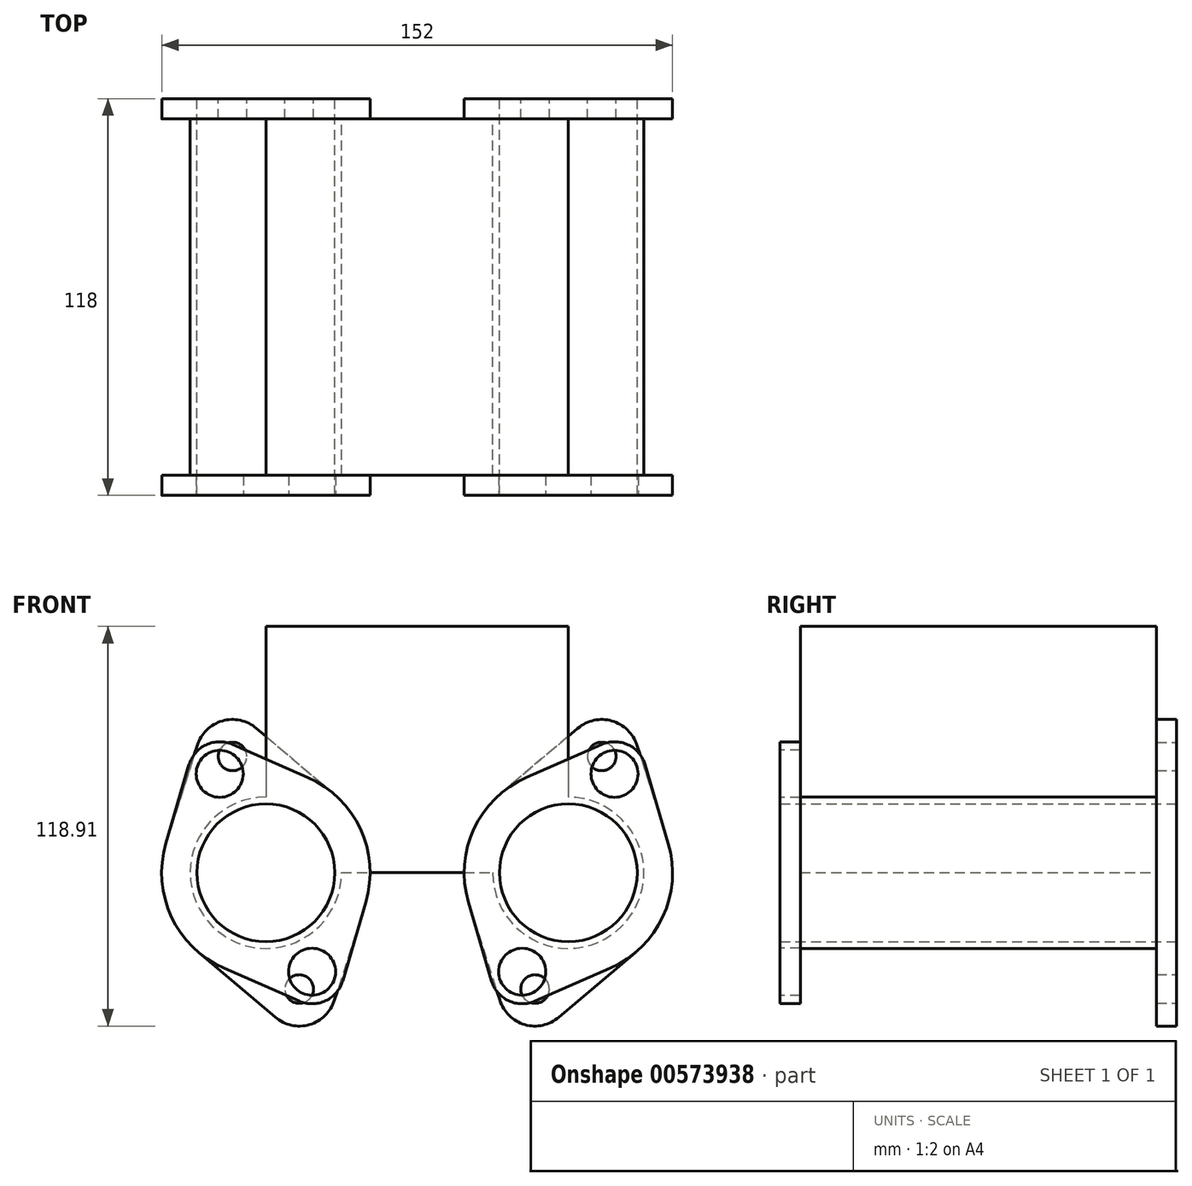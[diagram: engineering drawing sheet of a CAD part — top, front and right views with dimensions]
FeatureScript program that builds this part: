
annotation { "Feature Type Name" : "Feature", "Feature Type Description" : "" }
export const myFeature = defineFeature(function(context is Context, id is Id, definition is map)
    precondition{}
    {
        {
            var Q0;
            Q0=qCreatedBy(makeId("Front.planeOp"),FACE);
            var sketch = newSketch(context, id + "F0", { "sketchPlane" : qUnion([Q0])});
            skCircle(sketch, "E0", {"center": v(-45, 0) * mm, "radius": 20.5 * mm});
            skLineSegment(sketch, "E1", {"start": v(0, -41.53) * mm, "end": v(0, 36.5) * mm, "construction": true});
            skLineSegment(sketch, "E2", {"start": v(-45, -33.4) * mm, "end": v(-45, 27.72) * mm, "construction": true});
            skLineSegment(sketch, "E3", {"start": v(-35.08, -34.6) * mm, "end": v(-45, 0) * mm, "construction": true});
            skLineSegment(sketch, "E4", {"start": v(-45, 0) * mm, "end": v(-54.92, 34.6) * mm, "construction": true});
            skCircle(sketch, "E5", {"center": v(-54.92, 34.6) * mm, "radius": 4.25 * mm});
            skCircle(sketch, "E6", {"center": v(-35.08, -34.6) * mm, "radius": 4.25 * mm});
            skArc(sketch, "E7", {"start": v(-74.52, 9.45) * mm, "mid": v(-74.8, -8.54) * mm, "end": v(-65.03, -23.66) * mm});
            skArc(sketch, "E8", {"start": v(-42.18, -43) * mm, "mid": v(-32.05, -45.18) * mm, "end": v(-24.6, -37.96) * mm});
            skLineSegment(sketch, "E9", {"start": v(-65.4, 37.96) * mm, "end": v(-74.52, 9.45) * mm});
            skLineSegment(sketch, "E10", {"start": v(-47.82, 43) * mm, "end": v(-24.97, 23.66) * mm});
            skArc(sketch, "E11.trimOffspring", {"start": v(-47.82, 43) * mm, "mid": v(-57.95, 45.18) * mm, "end": v(-65.4, 37.96) * mm});
            skLineSegment(sketch, "E12", {"start": v(-42.18, -43) * mm, "end": v(-65.03, -23.66) * mm});
            skLineSegment(sketch, "E13", {"start": v(-15.48, -9.45) * mm, "end": v(-24.6, -37.96) * mm});
            skArc(sketch, "E14.trimOffspring", {"start": v(-15.48, -9.45) * mm, "mid": v(-15.2, 8.54) * mm, "end": v(-24.97, 23.66) * mm});
            skLineSegment(sketch, "E15.MirrorCS", {"start": v(45, 0) * mm, "end": v(54.92, 34.6) * mm, "construction": true});
            skCircle(sketch, "E16.MirrorC", {"center": v(35.08, -34.6) * mm, "radius": 4.25 * mm});
            skCircle(sketch, "E17.MirrorC", {"center": v(54.92, 34.6) * mm, "radius": 4.25 * mm});
            skLineSegment(sketch, "E18.MirrorCS", {"start": v(35.08, -34.6) * mm, "end": v(45, 0) * mm, "construction": true});
            skLineSegment(sketch, "E19.MirrorCS", {"start": v(15.48, -9.45) * mm, "end": v(24.6, -37.96) * mm});
            skArc(sketch, "E20.MirrorCS", {"start": v(15.48, -9.45) * mm, "mid": v(15.2, 8.54) * mm, "end": v(24.97, 23.66) * mm});
            skArc(sketch, "E21.MirrorCS", {"start": v(74.52, 9.45) * mm, "mid": v(74.8, -8.54) * mm, "end": v(65.03, -23.66) * mm});
            skCircle(sketch, "E22.MirrorC", {"center": v(45, 0) * mm, "radius": 20.5 * mm});
            skArc(sketch, "E23.MirrorCS", {"start": v(42.18, -43) * mm, "mid": v(32.05, -45.18) * mm, "end": v(24.6, -37.96) * mm});
            skLineSegment(sketch, "E24.MirrorCS", {"start": v(65.4, 37.96) * mm, "end": v(74.52, 9.45) * mm});
            skLineSegment(sketch, "E25.MirrorCS", {"start": v(47.82, 43) * mm, "end": v(24.97, 23.66) * mm});
            skArc(sketch, "E26.MirrorCS", {"start": v(47.82, 43) * mm, "mid": v(57.95, 45.18) * mm, "end": v(65.4, 37.96) * mm});
            skLineSegment(sketch, "E27.MirrorCS", {"start": v(42.18, -43) * mm, "end": v(65.03, -23.66) * mm});
            skLineSegment(sketch, "E28.MirrorCS", {"start": v(45, -33.4) * mm, "end": v(45, 27.72) * mm, "construction": true});
            skLineSegment(sketch, "E29", {"start": v(86.9, 0) * mm, "end": v(-90.5, 0) * mm, "construction": true});
            skSolve(sketch);
        }
        {
            var Q0;
            Q0 = qSketchRegion(id + "F0", true);
            extrude(context, id + "F1", {"entities" : qUnion([Q0]), "depth" : 6 * mm, "offsetDistance" : 25.4 * mm});
        }
        {
            var Q0;
            Q0=qCreatedBy(makeId("Front.planeOp"),FACE);
            cPlane(context, id + "F2", {"entities" : qUnion([Q0]), "cplaneType" : CPlaneType.OFFSET, "offset" : 118 * mm, "width" : 152.4 * mm, "height" : 152.4 * mm});
        }
        {
            var Q0;
            Q0=qCreatedBy(id+"F2.planeOp",FACE);
            var sketch = newSketch(context, id + "F3", { "sketchPlane" : qUnion([Q0])});
            skCircle(sketch, "E30.0", {"center": v(45, 0) * mm, "radius": 20.5 * mm, "construction": true});
            skCircle(sketch, "E31", {"center": v(45, 0) * mm, "radius": 22.5 * mm});
            skLineSegment(sketch, "E32", {"start": v(17.84, -58.24) * mm, "end": v(73.88, 61.93) * mm, "construction": true});
            skLineSegment(sketch, "E33", {"start": v(0, -102.35) * mm, "end": v(0, 115.75) * mm, "construction": true});
            skLineSegment(sketch, "E34", {"start": v(45, -103.34) * mm, "end": v(45, 115.75) * mm, "construction": true});
            skCircle(sketch, "E35", {"center": v(31.26, -29.46) * mm, "radius": 7 * mm});
            skCircle(sketch, "E36", {"center": v(58.74, 29.46) * mm, "radius": 7 * mm});
            skArc(sketch, "E37", {"start": v(22.13, -32.14) * mm, "mid": v(27.24, -38.09) * mm, "end": v(35.08, -38.18) * mm});
            skArc(sketch, "E38", {"start": v(67.87, 32.14) * mm, "mid": v(62.76, 38.09) * mm, "end": v(54.92, 38.18) * mm});
            skLineSegment(sketch, "E39", {"start": v(15.25, -8.73) * mm, "end": v(22.13, -32.14) * mm});
            skLineSegment(sketch, "E40.MirrorCS", {"start": v(57.43, -28.4) * mm, "end": v(35.08, -38.18) * mm});
            skLineSegment(sketch, "E41", {"start": v(45, 0) * mm, "end": v(73.1, -13.1) * mm, "construction": true});
            skLineSegment(sketch, "E42.MirrorCS", {"start": v(74.75, 8.73) * mm, "end": v(67.87, 32.14) * mm});
            skLineSegment(sketch, "E43.MirrorCS", {"start": v(32.57, 28.4) * mm, "end": v(54.92, 38.18) * mm});
            skArc(sketch, "E44.trimOffspring", {"start": v(57.43, -28.4) * mm, "mid": v(73.1, -13.1) * mm, "end": v(74.75, 8.73) * mm});
            skArc(sketch, "E45.trimOffspring", {"start": v(32.57, 28.4) * mm, "mid": v(16.9, 13.1) * mm, "end": v(15.25, -8.73) * mm});
            skArc(sketch, "E46.MirrorCS", {"start": v(-67.87, 32.14) * mm, "mid": v(-62.76, 38.09) * mm, "end": v(-54.92, 38.18) * mm});
            skArc(sketch, "E47.MirrorCS", {"start": v(-22.13, -32.14) * mm, "mid": v(-27.24, -38.09) * mm, "end": v(-35.08, -38.18) * mm});
            skArc(sketch, "E48.MirrorCS", {"start": v(-32.57, 28.4) * mm, "mid": v(-16.9, 13.1) * mm, "end": v(-15.25, -8.73) * mm});
            skCircle(sketch, "E49.MirrorC", {"center": v(-58.74, 29.46) * mm, "radius": 7 * mm});
            skArc(sketch, "E50.MirrorCS", {"start": v(-57.43, -28.4) * mm, "mid": v(-73.1, -13.1) * mm, "end": v(-74.75, 8.73) * mm});
            skCircle(sketch, "E51.MirrorC", {"center": v(-31.26, -29.46) * mm, "radius": 7 * mm});
            skLineSegment(sketch, "E52.MirrorCS", {"start": v(-32.57, 28.4) * mm, "end": v(-54.92, 38.18) * mm});
            skCircle(sketch, "E53.MirrorC", {"center": v(-45, 0) * mm, "radius": 20.5 * mm, "construction": true});
            skLineSegment(sketch, "E54.MirrorCS", {"start": v(-45, -103.34) * mm, "end": v(-45, 115.75) * mm, "construction": true});
            skLineSegment(sketch, "E55.MirrorCS", {"start": v(-17.84, -58.24) * mm, "end": v(-73.88, 61.93) * mm, "construction": true});
            skCircle(sketch, "E56.MirrorC", {"center": v(-45, 0) * mm, "radius": 22.5 * mm});
            skLineSegment(sketch, "E57.MirrorCS", {"start": v(-45, 0) * mm, "end": v(-73.1, -13.1) * mm, "construction": true});
            skLineSegment(sketch, "E58.MirrorCS", {"start": v(-57.43, -28.4) * mm, "end": v(-35.08, -38.18) * mm});
            skLineSegment(sketch, "E59.MirrorCS", {"start": v(-15.25, -8.73) * mm, "end": v(-22.13, -32.14) * mm});
            skLineSegment(sketch, "E60.MirrorCS", {"start": v(-74.75, 8.73) * mm, "end": v(-67.87, 32.14) * mm});
            skSolve(sketch);
        }
        {
            var Q0;
            Q0 = qSketchRegion(id + "F3", true);
            extrude(context, id + "F4", {"entities" : qUnion([Q0]), "oppositeDirection" : true, "depth" : 6 * mm, "offsetDistance" : 25.4 * mm});
        }
        {
            var Q0;
            Q0=makeQuery(id+"F1.opExtrude","CAP_FACE",FACE,{"disambiguationData":[OSD([sQuery(id+"F0.wireOp",EDGE,"E0"),sQuery(id+"F0.wireOp",EDGE,"E5"),sQuery(id+"F0.wireOp",EDGE,"E6"),sQuery(id+"F0.wireOp",EDGE,"E7"),sQuery(id+"F0.wireOp",EDGE,"E8"),sQuery(id+"F0.wireOp",EDGE,"E9"),sQuery(id+"F0.wireOp",EDGE,"E10"),sQuery(id+"F0.wireOp",EDGE,"E11.trimOffspring"),sQuery(id+"F0.wireOp",EDGE,"E12"),sQuery(id+"F0.wireOp",EDGE,"E13"),sQuery(id+"F0.wireOp",EDGE,"E14.trimOffspring")])],"isStart":false});
            var sketch = newSketch(context, id + "F5", { "sketchPlane" : qUnion([Q0])});
            skCircle(sketch, "E61.0", {"center": v(-45, 0) * mm, "radius": 20.5 * mm});
            skCircle(sketch, "E62.0", {"center": v(45, 0) * mm, "radius": 20.5 * mm});
            skCircle(sketch, "E63.0", {"center": v(-45, 0) * mm, "radius": 22.5 * mm});
            skCircle(sketch, "E64.0", {"center": v(45, 0) * mm, "radius": 22.5 * mm});
            skSolve(sketch);
        }
        {
            var Q0;
            Q0 = qSketchRegion(id + "F5", true);
            var Q1;
            Q1=makeQuery(id+"F4.opExtrude","CAP_FACE",FACE,{"disambiguationData":[OSD([sQuery(id+"F3.wireOp",EDGE,"E46.MirrorCS"),sQuery(id+"F3.wireOp",EDGE,"E47.MirrorCS"),sQuery(id+"F3.wireOp",EDGE,"E48.MirrorCS"),sQuery(id+"F3.wireOp",EDGE,"E49.MirrorC"),sQuery(id+"F3.wireOp",EDGE,"E50.MirrorCS"),sQuery(id+"F3.wireOp",EDGE,"E51.MirrorC"),sQuery(id+"F3.wireOp",EDGE,"E52.MirrorCS"),sQuery(id+"F3.wireOp",EDGE,"E56.MirrorC"),sQuery(id+"F3.wireOp",EDGE,"E58.MirrorCS"),sQuery(id+"F3.wireOp",EDGE,"E59.MirrorCS"),sQuery(id+"F3.wireOp",EDGE,"E60.MirrorCS")])],"isStart":true});
            extrude(context, id + "F6", {"entities" : qUnion([Q0]), "endBound" : BoundingType.UP_TO_SURFACE, "depth" : 25.4 * mm, "endBoundEntityFace" : qUnion([Q1]), "offsetDistance" : 25.4 * mm});
        }
        {
            var Q0;
            Q0=makeQuery(id+"F6.opExtrude","SWEPT_BODY",BODY,{"disambiguationData":[OSD([sQuery(id+"F5.wireOp",EDGE,"E62.0"),sQuery(id+"F5.wireOp",EDGE,"E64.0")])]});
            var Q1;
            Q1=makeQuery(id+"F4.opExtrude","SWEPT_BODY",BODY,{"disambiguationData":[OSD([sQuery(id+"F3.wireOp",EDGE,"E31"),sQuery(id+"F3.wireOp",EDGE,"E35"),sQuery(id+"F3.wireOp",EDGE,"E36"),sQuery(id+"F3.wireOp",EDGE,"E37"),sQuery(id+"F3.wireOp",EDGE,"E38"),sQuery(id+"F3.wireOp",EDGE,"E39"),sQuery(id+"F3.wireOp",EDGE,"E40.MirrorCS"),sQuery(id+"F3.wireOp",EDGE,"E42.MirrorCS"),sQuery(id+"F3.wireOp",EDGE,"E43.MirrorCS"),sQuery(id+"F3.wireOp",EDGE,"E44.trimOffspring"),sQuery(id+"F3.wireOp",EDGE,"E45.trimOffspring")])]});
            booleanBodies(context, id + "F7", {"operationType" : BooleanOperationType.UNION, "tools" : qUnion([Q0, Q1])});
        }
        {
            var Q0;
            Q0=makeQuery(id+"F1.opExtrude","CAP_FACE",FACE,{"disambiguationData":[OSD([sQuery(id+"F0.wireOp",EDGE,"E0"),sQuery(id+"F0.wireOp",EDGE,"E5"),sQuery(id+"F0.wireOp",EDGE,"E6"),sQuery(id+"F0.wireOp",EDGE,"E7"),sQuery(id+"F0.wireOp",EDGE,"E8"),sQuery(id+"F0.wireOp",EDGE,"E9"),sQuery(id+"F0.wireOp",EDGE,"E10"),sQuery(id+"F0.wireOp",EDGE,"E11.trimOffspring"),sQuery(id+"F0.wireOp",EDGE,"E12"),sQuery(id+"F0.wireOp",EDGE,"E13"),sQuery(id+"F0.wireOp",EDGE,"E14.trimOffspring")])],"isStart":false});
            var sketch = newSketch(context, id + "F8", { "sketchPlane" : qUnion([Q0])});
            skArc(sketch, "E65.0", {"start": v(-22.5, 0) * mm, "mid": v(-29.1, 15.9) * mm, "end": v(-45, 22.5) * mm});
            skArc(sketch, "E66.0", {"start": v(45, 22.5) * mm, "mid": v(29.1, 15.9) * mm, "end": v(22.5, 0) * mm});
            skLineSegment(sketch, "E67", {"start": v(-45, 22.5) * mm, "end": v(45, 22.5) * mm});
            skLineSegment(sketch, "E68", {"start": v(-22.5, 0) * mm, "end": v(22.5, 0) * mm});
            skSolve(sketch);
        }
        {
            var Q0;
            Q0 = qSketchRegion(id + "F8", true);
            var Q1;
            Q1=makeQuery(id+"F4.opExtrude","CAP_FACE",FACE,{"disambiguationData":[OSD([sQuery(id+"F3.wireOp",EDGE,"E46.MirrorCS"),sQuery(id+"F3.wireOp",EDGE,"E47.MirrorCS"),sQuery(id+"F3.wireOp",EDGE,"E48.MirrorCS"),sQuery(id+"F3.wireOp",EDGE,"E49.MirrorC"),sQuery(id+"F3.wireOp",EDGE,"E50.MirrorCS"),sQuery(id+"F3.wireOp",EDGE,"E51.MirrorC"),sQuery(id+"F3.wireOp",EDGE,"E52.MirrorCS"),sQuery(id+"F3.wireOp",EDGE,"E56.MirrorC"),sQuery(id+"F3.wireOp",EDGE,"E58.MirrorCS"),sQuery(id+"F3.wireOp",EDGE,"E59.MirrorCS"),sQuery(id+"F3.wireOp",EDGE,"E60.MirrorCS")])],"isStart":false});
            extrude(context, id + "F9", {"entities" : qUnion([Q0]), "operationType" : NewBodyOperationType.ADD, "endBound" : BoundingType.UP_TO_SURFACE, "depth" : 25.4 * mm, "endBoundEntityFace" : qUnion([Q1]), "offsetDistance" : 25.4 * mm});
        }
        {
            var Q0;
            Q0=makeQuery(id+"F9.opExtrude","SWEPT_FACE",FACE,{"disambiguationData":[OSD([sQuery(id+"F8.wireOp",EDGE,"E67")])]});
            extrude(context, id + "F10", {"entities" : qUnion([Q0]), "operationType" : NewBodyOperationType.ADD, "depth" : 50.8 * mm, "offsetDistance" : 25.4 * mm});
        }
    });
